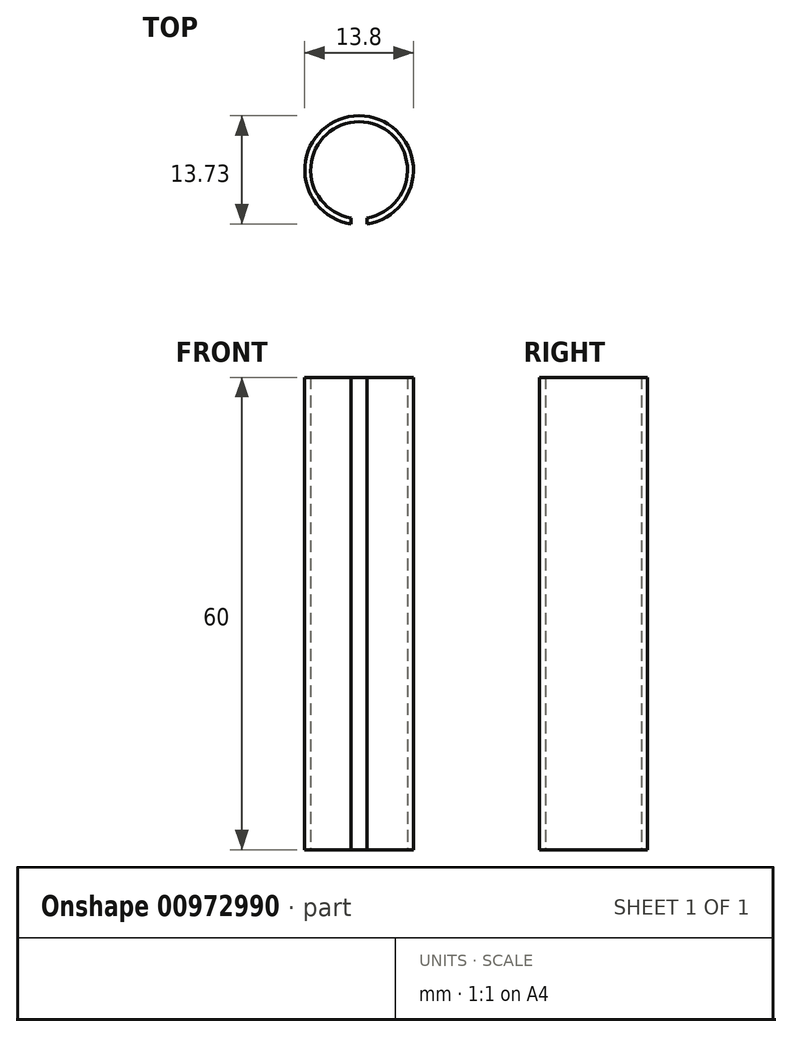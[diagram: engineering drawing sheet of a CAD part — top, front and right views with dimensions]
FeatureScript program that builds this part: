
annotation { "Feature Type Name" : "Feature", "Feature Type Description" : "" }
export const myFeature = defineFeature(function(context is Context, id is Id, definition is map)
    precondition{}
    {
        {
            var Q0;
            Q0=qCreatedBy(makeId("Top.planeOp"),FACE);
            var sketch = newSketch(context, id + "F0", { "sketchPlane" : qUnion([Q0])});
            skArc(sketch, "E0", {"start": v(1, -6.07) * mm, "mid": v(0, 6.15) * mm, "end": v(-1, -6.07) * mm});
            skArc(sketch, "E1", {"start": v(1, -6.83) * mm, "mid": v(0, 6.9) * mm, "end": v(-1, -6.83) * mm});
            skLineSegment(sketch, "E2", {"start": v(0, -4.63) * mm, "end": v(0, -10.14) * mm, "construction": true});
            skLineSegment(sketch, "E3.0", {"start": v(-1, -6.07) * mm, "end": v(-1, -6.83) * mm});
            skLineSegment(sketch, "E4.0", {"start": v(1, -6.07) * mm, "end": v(1, -6.83) * mm});
            skSolve(sketch);
        }
        {
            var Q0;
            Q0 = qSketchRegion(id + "F0", true);
            extrude(context, id + "F1", {"entities" : qUnion([Q0]), "depth" : 60 * mm, "offsetDistance" : 25 * mm});
        }
    });
